# Revit family: RN 91030 Optifitt-Serra-Verschlusszapfen
name_source: partatom
category: Rohrformteile
units: mm (PartAtom-declared; Revit-internal decimal feet)

## family parameters
Arbeitsebenenbasiert = Nein
Beim Laden mit Abzugskörper schneiden = Nein
Bemaßung runder Anschluss = Durchmesser verwenden
Gemeinsam genutzt = Nein
Immer vertikal = Ja
Teiletyp = Nicht definiert

## types (5) — shared parameters
1.010.00.2 Blattnummer der Richtlinie = 29
1.010.00.3 Ausgabedatum (Monat) der Richtlinie = 201308
1.010.00.4 Herstellername = R. Nussbaum AG
1.010.00.5 Revisionsdatum der Datei = 20190521
1.010.00.6 Webadresse des Herstellers = http://www.nussbaum.ch
1.100.00.4 Produktbezeichnung = Versorgung
1.110.00.2 Index = 3
1.110.00.4 Produktbezeichnung = Optifitt-Serra
1.960/3L.00.8 Link (URL) = https://www.nussbaum.ch
29.700.00.4 Produktname = Optifitt-Serra-Verschlusszapfen
29.700.00.5 Produktkennung = 2
29.700.00.6 Querschnittsform = 1
29.700.00.7 Nennweitensystem = DN
29.700.00.8 Nenndrucksystem = PN
29.710.02.4 Nenndruck = 16
29.710.02.5 max. zul. Überdruck [hPa] = 1600
29.710.02.7 max. zul. Dauer-Betriebsdruck [hPa] = 1600
29.710.02.9 max. zul. Dauer-Betriebstemperatur [°C] = 90
Connector Visibility = Nein
EnclosingSpace Visibility = Nein
Hersteller = R. Nussbaum AG
URL = https://www.nussbaum.ch

## per-type parameters (varying)
| type | 1.800.00.3 TGA-Nummer | 1.800.00.4 Kommentarfeld | 1.810.00.3 Hersteller-Bestellnummer | 1.810.00.4 DATANORM-Nummer | 1.810.00.5 StLB-Nummer | 1.810.00.6 GTIN-Nummer | 29.710.02.10 Formstück-Gewicht [kg] | 29.710.02.3 Benennung | CONNECTOR0_DIAMETER_dX_0r | CONNECTOR0_dX_01 | CONNECTOR0_ref_dX | Modell | R. Nussbaum AG 91030.52 de Visibility | R. Nussbaum AG 91030.53 de Visibility | R. Nussbaum AG 91030.54 de Visibility | R. Nussbaum AG 91030.55 de Visibility | R. Nussbaum AG 91030.56 de Visibility | Typenkommentare |
| DN=25 | 01900300000000000000000000000000000000000000000022000000000000000026 | 91030.56, Optifitt-Serra-Verschlusszapfen, DN=25, L=19 | 91030.56 | 91030.56 | 216.114 | 7612945036131 | 0.062 | Optifitt-Serra-Verschlusszapfen, DN=25, L=19 | 25 mm  [stored 0.082021 ft] | 9 mm | 9 mm | 91030.56 | Nein | Nein | Nein | Nein | Ja | Optifitt-Serra-Verschlusszapfen  DN=25 |
| DN=20 | 01900300000000000000000000000000000000000000000022000000000000000025 | 91030.55, Optifitt-Serra-Verschlusszapfen, DN=20, L=18 | 91030.55 | 91030.55 | 216.113 | 7612945036124 | 0.04 | Optifitt-Serra-Verschlusszapfen, DN=20, L=18 | 20 mm | 8 mm  [stored 0.0262467 ft] | 8 mm  [stored 0.0262467 ft] | 91030.55 | Nein | Nein | Nein | Ja | Nein | Optifitt-Serra-Verschlusszapfen  DN=20 |
| DN=15 | 01900300000000000000000000000000000000000000000022000000000000000024 | 91030.54, Optifitt-Serra-Verschlusszapfen, DN=15, L=18 | 91030.54 | 91030.54 | 216.112 | 7612945036117 | 0.027 | Optifitt-Serra-Verschlusszapfen, DN=15, L=18 | 15 mm | 8 mm  [stored 0.0262467 ft] | 8 mm  [stored 0.0262467 ft] | 91030.54 | Nein | Nein | Ja | Nein | Nein | Optifitt-Serra-Verschlusszapfen  DN=15 |
| DN=1 | 01900300000000000000000000000000000000000000000022000000000000000023 | 91030.53, Optifitt-Serra-Verschlusszapfen, DN=10, L=16 | 91030.53 | 91030.53 | 216.111 | 7612945036100 | 0.021 | Optifitt-Serra-Verschlusszapfen, DN=10, L=16 | 10 mm  [stored 0.0328084 ft] | 8 mm  [stored 0.0262467 ft] | 8 mm  [stored 0.0262467 ft] | 91030.53 | Nein | Ja | Nein | Nein | Nein | Optifitt-Serra-Verschlusszapfen  DN=10 |
| DN=10 | 01900300000000000000000000000000000000000000000022000000000000000022 | 91030.52, Optifitt-Serra-Verschlusszapfen, DN=10, L=14 | 91030.52 | 91030.52 |  | 7612945036094 | 0.008 | Optifitt-Serra-Verschlusszapfen, DN=10, L=14 | 8 mm  [stored 0.0262467 ft] | 7 mm  [stored 0.0229659 ft] | 7 mm  [stored 0.0229659 ft] | 91030.52 | Ja | Nein | Nein | Nein | Nein | Optifitt-Serra-Verschlusszapfen  DN=10 |

note: [stored X ft] marks values corroborated as IEEE doubles in the binary element streams (Revit-internal decimal feet)

## geometry (parser evidence)
native form markers: Sweep x2
no freeform markers — native parametric forms only
